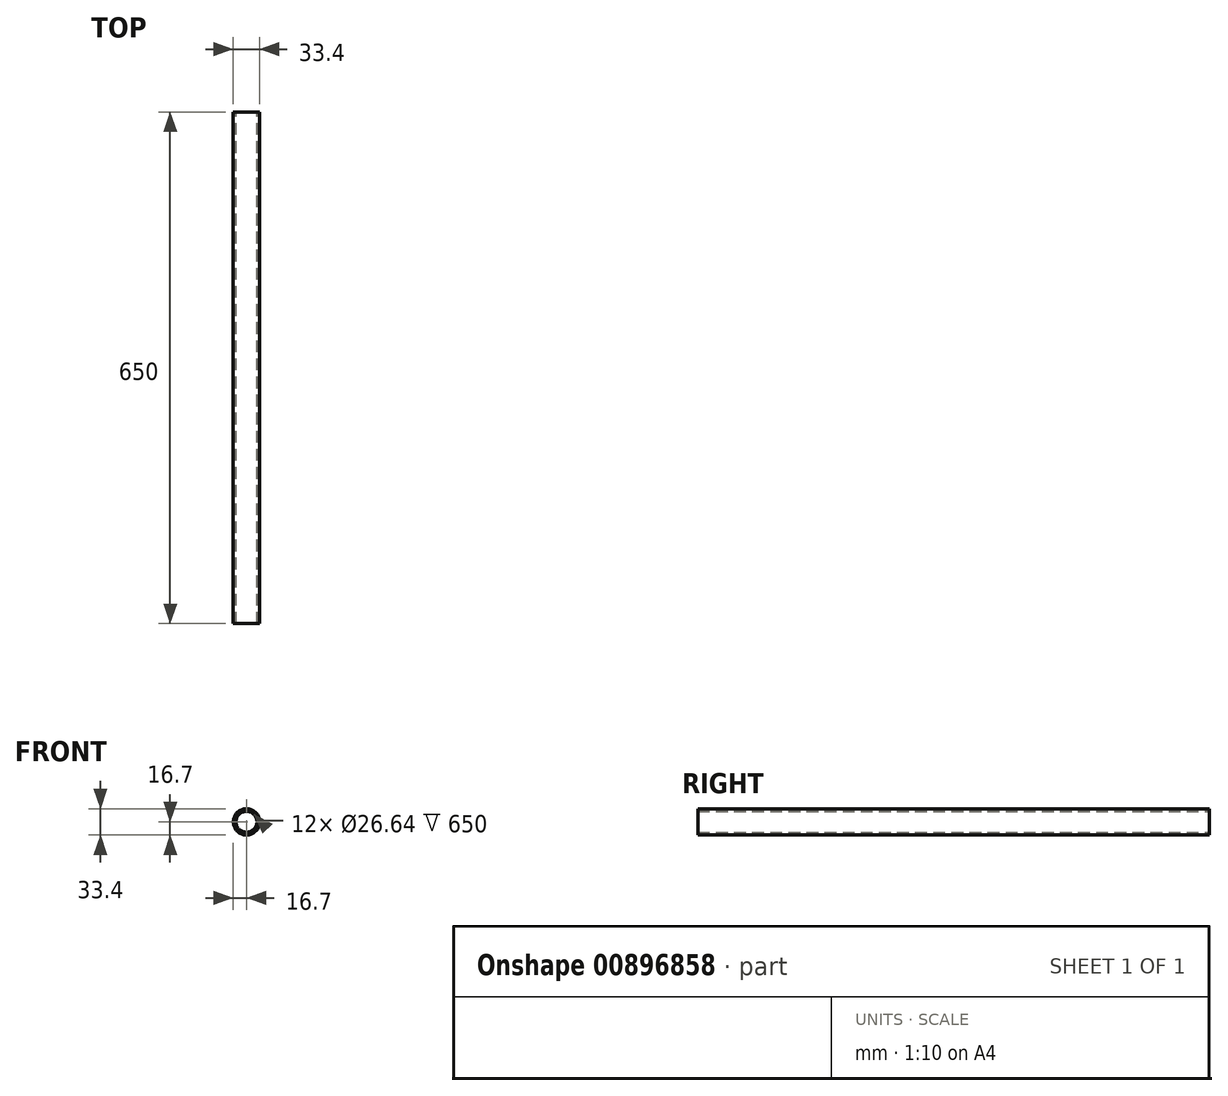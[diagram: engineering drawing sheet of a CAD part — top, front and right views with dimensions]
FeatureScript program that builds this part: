
annotation { "Feature Type Name" : "Feature", "Feature Type Description" : "" }
export const myFeature = defineFeature(function(context is Context, id is Id, definition is map)
    precondition{}
    {
        {
            var Q0;
            Q0=qCreatedBy(makeId("Front.planeOp"),FACE);
            var sketch = newSketch(context, id + "F0", { "sketchPlane" : qUnion([Q0])});
            skCircle(sketch, "E0", {"center": v(0, 0) * mm, "radius": 16.7 * mm});
            skCircle(sketch, "E1", {"center": v(0, 0) * mm, "radius": 13.32 * mm});
            skSolve(sketch);
        }
        {
            var Q0;
            Q0=makeQuery(id+"F0.imprint","IMPRINT",FACE,{"disambiguationData":[TD([[makeQuery(id+"F0.imprint","IMPRINT",EDGE,{"derivedFrom":sQuery(id+"F0.wireOp",EDGE,"E0")}),1.0]])]});
            extrude(context, id + "F1", {"entities" : qUnion([Q0]), "endBound" : BoundingType.SYMMETRIC, "depth" : 650 * mm, "offsetDistance" : 25.4 * mm});
        }
    });
